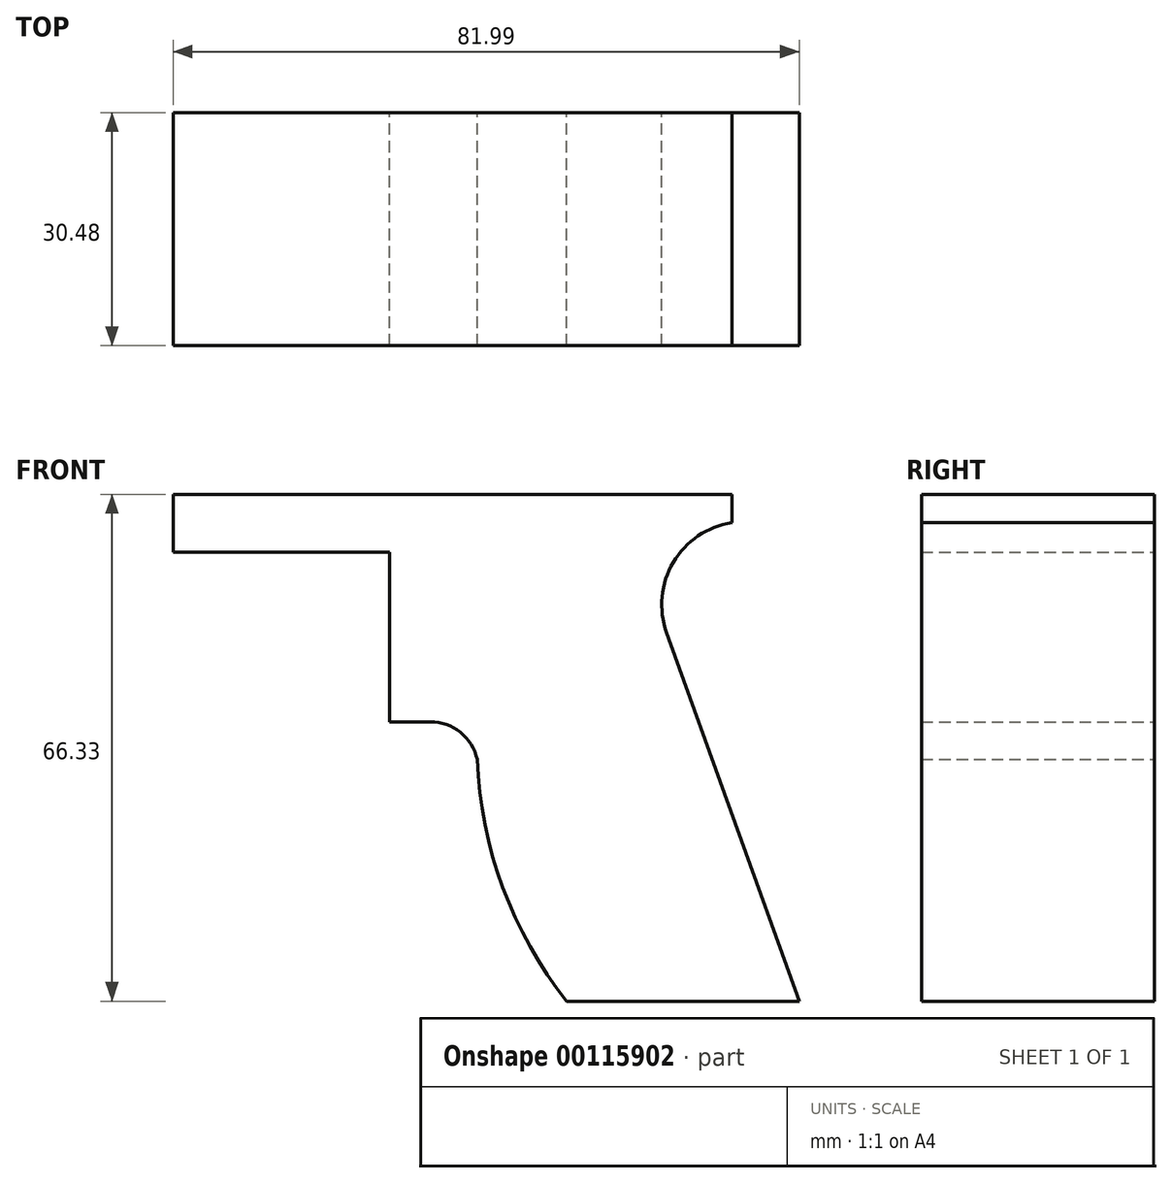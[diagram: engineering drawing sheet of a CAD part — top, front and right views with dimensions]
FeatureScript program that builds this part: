
annotation { "Feature Type Name" : "Feature", "Feature Type Description" : "" }
export const myFeature = defineFeature(function(context is Context, id is Id, definition is map)
    precondition{}
    {
        {
            var Q0;
            Q0=qCreatedBy(makeId("Front.planeOp"),FACE);
            var sketch = newSketch(context, id + "F0", { "sketchPlane" : qUnion([Q0])});
            skLineSegment(sketch, "E0", {"start": v(51.51, -66.33) * mm, "end": v(82, -66.33) * mm});
            skLineSegment(sketch, "E1", {"start": v(82, -66.33) * mm, "end": v(64.62, -18.1) * mm});
            skArc(sketch, "E2", {"start": v(73.16, -3.69) * mm, "mid": v(65.5, -8.88) * mm, "end": v(64.62, -18.1) * mm});
            skArc(sketch, "E3", {"start": v(39.82, -34.68) * mm, "mid": v(43.15, -51.43) * mm, "end": v(51.51, -66.33) * mm});
            skArc(sketch, "E4", {"start": v(39.82, -34.68) * mm, "mid": v(37.6, -31.13) * mm, "end": v(33.65, -29.75) * mm});
            skLineSegment(sketch, "E5", {"start": v(33.65, -29.75) * mm, "end": v(28.34, -29.75) * mm});
            skPoint(sketch, "E5.endSnap0", {"position": v(37.6, -31.13) * mm});
            skLineSegment(sketch, "E6", {"start": v(28.34, -29.75) * mm, "end": v(28.34, -7.54) * mm});
            skLineSegment(sketch, "E7", {"start": v(28.34, -7.54) * mm, "end": v(0, -7.54) * mm});
            skLineSegment(sketch, "E8", {"start": v(0, -7.54) * mm, "end": v(0, 0) * mm});
            skLineSegment(sketch, "E9", {"start": v(0, 0) * mm, "end": v(73.16, 0) * mm});
            skLineSegment(sketch, "E10", {"start": v(73.16, 0) * mm, "end": v(73.16, -3.69) * mm});
            skSolve(sketch);
        }
        {
            var Q0;
            Q0=makeQuery(id+"F0.imprint","IMPRINT",FACE,{"disambiguationData":[TD([[makeQuery(id+"F0.imprint","IMPRINT",EDGE,{"derivedFrom":sQuery(id+"F0.wireOp",EDGE,"E0")}),1.0]])]});
            extrude(context, id + "F1", {"entities" : qUnion([Q0]), "endBound" : BoundingType.SYMMETRIC, "depth" : 30.48 * mm});
        }
    });
